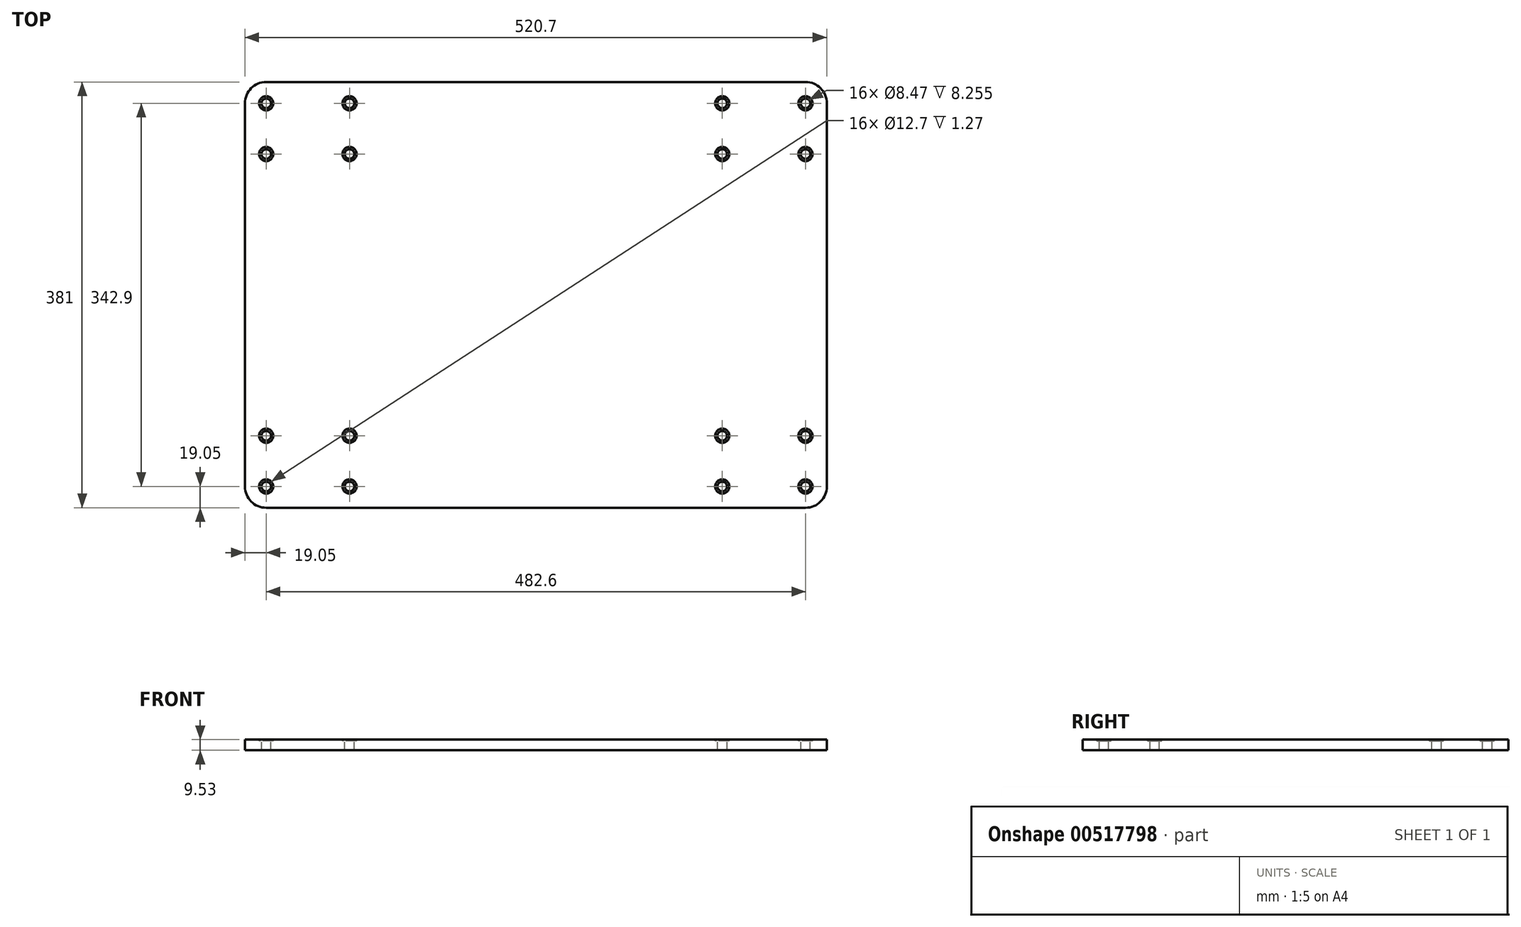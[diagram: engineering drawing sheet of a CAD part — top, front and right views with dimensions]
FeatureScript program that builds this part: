
annotation { "Feature Type Name" : "Feature", "Feature Type Description" : "" }
export const myFeature = defineFeature(function(context is Context, id is Id, definition is map)
    precondition{}
    {
        {
            var Q0;
            Q0=qCreatedBy(makeId("Top.planeOp"),FACE);
            var sketch = newSketch(context, id + "F0", { "sketchPlane" : qUnion([Q0])});
            skPoint(sketch, "E0.middle", {"position": v(0, 0) * mm});
            skLineSegment(sketch, "E1.0", {"start": v(260.35, 171.45) * mm, "end": v(260.35, -171.45) * mm});
            skLineSegment(sketch, "E1.1", {"start": v(241.3, 190.5) * mm, "end": v(-241.3, 190.5) * mm});
            skLineSegment(sketch, "E1.2", {"start": v(-260.35, 171.45) * mm, "end": v(-260.35, -171.45) * mm});
            skLineSegment(sketch, "E1.3", {"start": v(241.3, -190.5) * mm, "end": v(-241.3, -190.5) * mm});
            skPoint(sketch, "E2.visualSharp", {"position": v(-260.35, 190.5) * mm});
            skArc(sketch, "E2.filletArc", {"start": v(-241.3, 190.5) * mm, "mid": v(-254.77, 184.92) * mm, "end": v(-260.35, 171.45) * mm});
            skPoint(sketch, "E3.visualSharp", {"position": v(260.35, 190.5) * mm});
            skArc(sketch, "E3.filletArc", {"start": v(260.35, 171.45) * mm, "mid": v(254.77, 184.92) * mm, "end": v(241.3, 190.5) * mm});
            skPoint(sketch, "E4.visualSharp", {"position": v(260.35, -190.5) * mm});
            skArc(sketch, "E4.filletArc", {"start": v(241.3, -190.5) * mm, "mid": v(254.77, -184.92) * mm, "end": v(260.35, -171.45) * mm});
            skPoint(sketch, "E5.visualSharp", {"position": v(-260.35, -190.5) * mm});
            skArc(sketch, "E5.filletArc", {"start": v(-260.35, -171.45) * mm, "mid": v(-254.77, -184.92) * mm, "end": v(-241.3, -190.5) * mm});
            skSolve(sketch);
        }
        {
            var Q0;
            Q0=makeQuery(id+"F0.imprint","IMPRINT",FACE,{"disambiguationData":[TD([[makeQuery(id+"F0.imprint","IMPRINT",EDGE,{"derivedFrom":sQuery(id+"F0.wireOp",EDGE,"E1.0")}),-1.0]])]});
            extrude(context, id + "F1", {"entities" : qUnion([Q0]), "depth" : 9.52 * mm, "offsetDistance" : 25.4 * mm});
        }
        {
            var Q0;
            Q0=makeQuery(id+"F1.opExtrude","CAP_FACE",FACE,{"disambiguationData":[OSD([sQuery(id+"F0.wireOp",EDGE,"E1.0"),sQuery(id+"F0.wireOp",EDGE,"E1.1"),sQuery(id+"F0.wireOp",EDGE,"E1.2"),sQuery(id+"F0.wireOp",EDGE,"E1.3"),sQuery(id+"F0.wireOp",EDGE,"E2.filletArc"),sQuery(id+"F0.wireOp",EDGE,"E3.filletArc"),sQuery(id+"F0.wireOp",EDGE,"E4.filletArc"),sQuery(id+"F0.wireOp",EDGE,"E5.filletArc")])],"isStart":false});
            var sketch = newSketch(context, id + "F2", { "sketchPlane" : qUnion([Q0])});
            skPoint(sketch, "E6", {"position": v(-241.3, -171.45) * mm});
            skPoint(sketch, "E7.0.1.0", {"position": v(-241.3, -126.06) * mm});
            skPoint(sketch, "E7.1.0.0", {"position": v(-166.78, -171.45) * mm});
            skPoint(sketch, "E7.1.1.0", {"position": v(-166.78, -126.06) * mm});
            skLineSegment(sketch, "E7.direction1", {"start": v(-241.3, -171.45) * mm, "end": v(-166.78, -171.45) * mm, "construction": true});
            skLineSegment(sketch, "E7.direction2", {"start": v(-241.3, -171.45) * mm, "end": v(-241.3, -126.06) * mm, "construction": true});
            skPoint(sketch, "E8.MirrorP", {"position": v(-241.3, 171.45) * mm});
            skLineSegment(sketch, "E9.MirrorCS", {"start": v(-241.3, 171.45) * mm, "end": v(-241.3, 126.06) * mm, "construction": true});
            skLineSegment(sketch, "E10.MirrorCS", {"start": v(-241.3, 171.45) * mm, "end": v(-166.78, 171.45) * mm, "construction": true});
            skPoint(sketch, "E11.MirrorP", {"position": v(-166.78, 171.45) * mm});
            skPoint(sketch, "E12.MirrorP", {"position": v(-241.3, 126.06) * mm});
            skPoint(sketch, "E13.MirrorP", {"position": v(-166.78, 126.06) * mm});
            skLineSegment(sketch, "E14.MirrorCS", {"start": v(241.3, 171.45) * mm, "end": v(166.78, 171.45) * mm, "construction": true});
            skPoint(sketch, "E15.MirrorP", {"position": v(241.3, -171.45) * mm});
            skPoint(sketch, "E16.MirrorP", {"position": v(241.3, -126.06) * mm});
            skPoint(sketch, "E17.MirrorP", {"position": v(166.78, -171.45) * mm});
            skPoint(sketch, "E18.MirrorP", {"position": v(166.78, 126.06) * mm});
            skLineSegment(sketch, "E19.MirrorCS", {"start": v(241.3, -171.45) * mm, "end": v(241.3, -126.06) * mm, "construction": true});
            skPoint(sketch, "E20.MirrorP", {"position": v(241.3, 171.45) * mm});
            skLineSegment(sketch, "E21.MirrorCS", {"start": v(241.3, -171.45) * mm, "end": v(166.78, -171.45) * mm, "construction": true});
            skPoint(sketch, "E22.MirrorP", {"position": v(166.78, 171.45) * mm});
            skLineSegment(sketch, "E23.MirrorCS", {"start": v(241.3, 171.45) * mm, "end": v(241.3, 126.06) * mm, "construction": true});
            skPoint(sketch, "E24.MirrorP", {"position": v(166.78, -126.06) * mm});
            skPoint(sketch, "E25.MirrorP", {"position": v(241.3, 126.06) * mm});
            skSolve(sketch);
        }
        {
            var Q0;
            Q0=sQuery(id+"F0.wireOp",VERTEX,"E0.middle");
            var Q1;
            Q1=sQuery(id+"F0.wireOp",VERTEX,"E5.filletArc.center");
            var Q2;
            Q2=sQuery(id+"F0.wireOp",VERTEX,"E4.filletArc.center");
            var Q3;
            Q3=sQuery(id+"F0.wireOp",VERTEX,"E2.filletArc.center");
            var Q4;
            Q4=sQuery(id+"F0.wireOp",VERTEX,"E3.filletArc.center");
            var Q5;
            Q5=sQuery(id+"F2.wireOp",VERTEX,"E17.MirrorP");
            var Q6;
            Q6=sQuery(id+"F2.wireOp",VERTEX,"E12.MirrorP");
            var Q7;
            Q7=sQuery(id+"F2.wireOp",VERTEX,"E22.MirrorP");
            var Q8;
            Q8=sQuery(id+"F2.wireOp",VERTEX,"E24.MirrorP");
            var Q9;
            Q9=sQuery(id+"F2.wireOp",VERTEX,"E16.MirrorP");
            var Q10;
            Q10=sQuery(id+"F2.wireOp",VERTEX,"E20.MirrorP");
            var Q11;
            Q11=sQuery(id+"F2.wireOp",VERTEX,"E13.MirrorP");
            var Q12;
            Q12=sQuery(id+"F2.wireOp",VERTEX,"E6");
            var Q13;
            Q13=sQuery(id+"F2.wireOp",VERTEX,"E7.1.0.0");
            var Q14;
            Q14=sQuery(id+"F2.wireOp",VERTEX,"E7.1.1.0");
            var Q15;
            Q15=sQuery(id+"F2.wireOp",VERTEX,"E15.MirrorP");
            var Q16;
            Q16=sQuery(id+"F2.wireOp",VERTEX,"E18.MirrorP");
            var Q17;
            Q17=sQuery(id+"F2.wireOp",VERTEX,"E11.MirrorP");
            var Q18;
            Q18=sQuery(id+"F2.wireOp",VERTEX,"E25.MirrorP");
            var Q19;
            Q19=sQuery(id+"F2.wireOp",VERTEX,"E8.MirrorP");
            var Q20;
            Q20=sQuery(id+"F2.wireOp",VERTEX,"E7.0.1.0");
            var Q21;
            Q21=makeQuery(id+"F1.opExtrude","SWEPT_BODY",BODY,{"disambiguationData":[OSD([sQuery(id+"F0.wireOp",EDGE,"E1.0"),sQuery(id+"F0.wireOp",EDGE,"E1.1"),sQuery(id+"F0.wireOp",EDGE,"E1.2"),sQuery(id+"F0.wireOp",EDGE,"E1.3"),sQuery(id+"F0.wireOp",EDGE,"E2.filletArc"),sQuery(id+"F0.wireOp",EDGE,"E3.filletArc"),sQuery(id+"F0.wireOp",EDGE,"E4.filletArc"),sQuery(id+"F0.wireOp",EDGE,"E5.filletArc")])]});
            hole(context, id + "F3", {"style" : HoleStyle.C_BORE, "endStyle" : HoleEndStyle.THROUGH, "holeDiameter" : 8.47 * mm, "cBoreDiameter" : 12.7 * mm, "cBoreDepth" : 1.27 * mm, "isTappedThrough" : true, "tappedDepth" : 12.7 * mm, "tapClearance" : 3, "locations" : qUnion([Q0, Q1, Q2, Q3, Q4, Q5, Q6, Q7, Q8, Q9, Q10, Q11, Q12, Q13, Q14, Q15, Q16, Q17, Q18, Q19, Q20]), "scope" : qUnion([Q21])});
        }
    });
